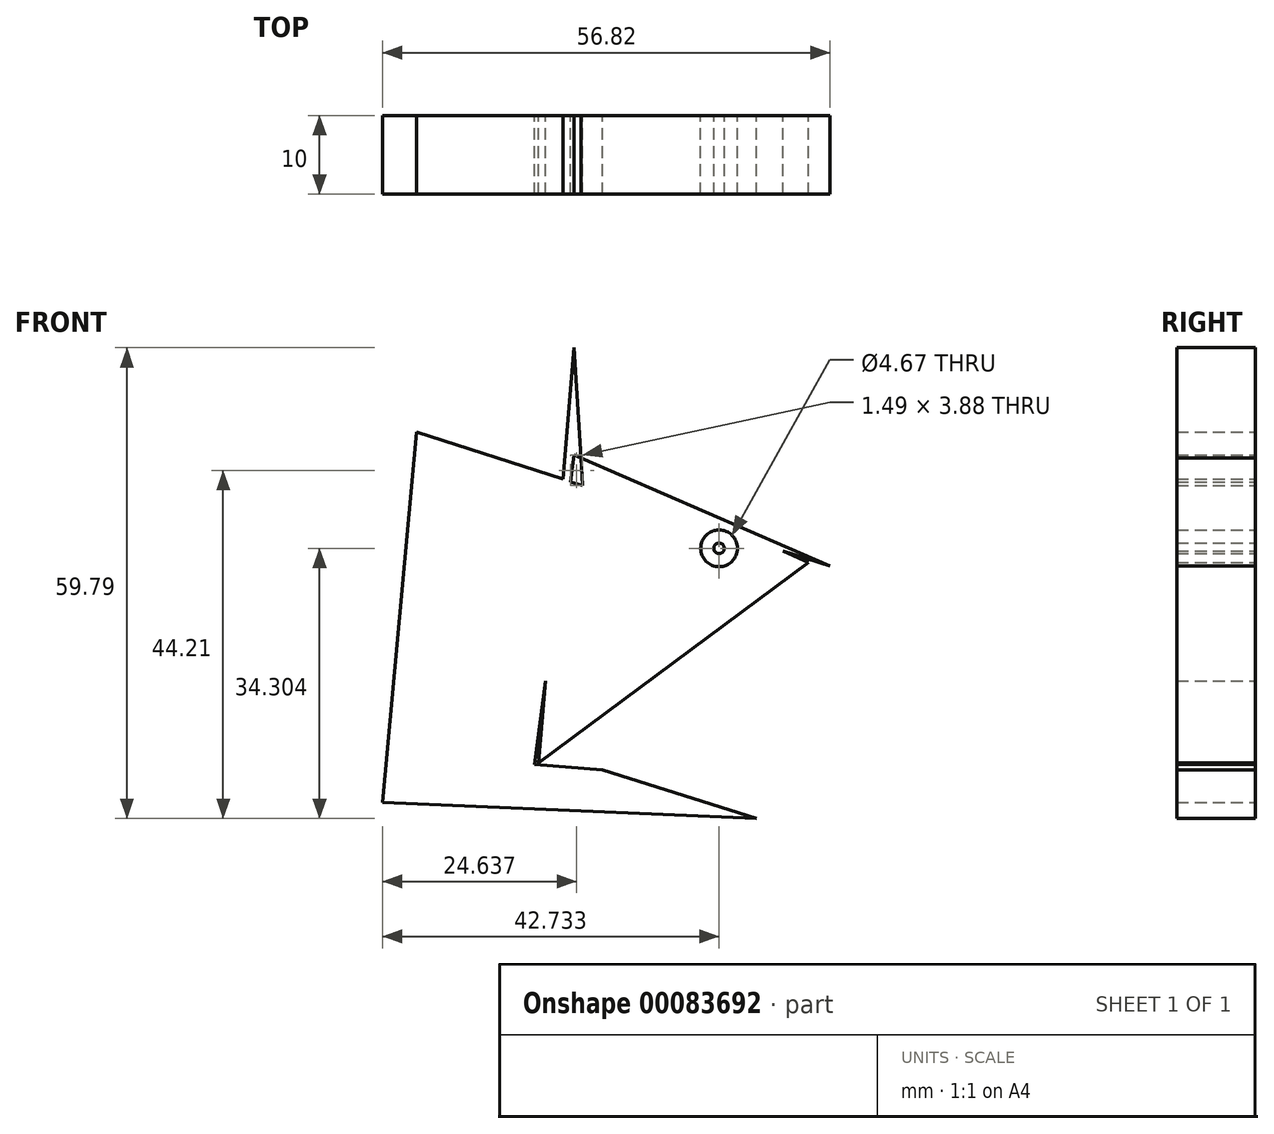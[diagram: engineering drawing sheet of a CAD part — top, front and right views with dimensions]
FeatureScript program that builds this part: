
annotation { "Feature Type Name" : "Feature", "Feature Type Description" : "" }
export const myFeature = defineFeature(function(context is Context, id is Id, definition is map)
    precondition{}
    {
        {
            var Q0;
            Q0=qCreatedBy(makeId("Front.planeOp"),FACE);
            var sketch = newSketch(context, id + "F0", { "sketchPlane" : qUnion([Q0])});
            skLineSegment(sketch, "E0", {"start": v(-28.64, 2.16) * mm, "end": v(-31.82, 54.67) * mm});
            skLineSegment(sketch, "E1", {"start": v(-31.82, 54.67) * mm, "end": v(-36.36, 1.93) * mm});
            skLineSegment(sketch, "E2", {"start": v(-36.36, 1.93) * mm, "end": v(-2.05, 27.4) * mm});
            skLineSegment(sketch, "E3", {"start": v(-2.05, 27.4) * mm, "end": v(-31.82, 41.03) * mm});
            skLineSegment(sketch, "E4", {"start": v(-31.82, 41.03) * mm, "end": v(0.68, 26.94) * mm});
            skLineSegment(sketch, "E5", {"start": v(0.68, 26.94) * mm, "end": v(-51.82, 43.99) * mm});
            skLineSegment(sketch, "E6", {"start": v(-51.82, 43.99) * mm, "end": v(-56.14, -3.07) * mm});
            skLineSegment(sketch, "E7", {"start": v(-56.14, -3.07) * mm, "end": v(-8.64, -5.12) * mm});
            skLineSegment(sketch, "E8", {"start": v(-8.64, -5.12) * mm, "end": v(-28.18, 1.02) * mm});
            skLineSegment(sketch, "E9", {"start": v(-28.18, 1.02) * mm, "end": v(-36.82, 1.7) * mm});
            skLineSegment(sketch, "E10", {"start": v(-36.82, 1.7) * mm, "end": v(-31.82, 41.03) * mm});
            skSolve(sketch);
        }
        {
            var Q0;
            Q0 = qSketchRegion(id + "F0", true);
            var Q1;
            Q1=sQuery(id+"F0.wireOp",EDGE,"E3");
            var Q2;
            Q2=sQuery(id+"F0.wireOp",EDGE,"E10");
            var Q3;
            Q3=sQuery(id+"F0.wireOp",EDGE,"E4");
            var Q4;
            Q4=sQuery(id+"F0.wireOp",EDGE,"E5");
            var Q5;
            Q5=sQuery(id+"F0.wireOp",EDGE,"E2");
            var Q6;
            Q6=sQuery(id+"F0.wireOp",EDGE,"E1");
            var Q7;
            Q7=sQuery(id+"F0.wireOp",EDGE,"E6");
            var Q8;
            Q8=sQuery(id+"F0.wireOp",EDGE,"E0");
            var Q9;
            Q9=sQuery(id+"F0.wireOp",EDGE,"E7");
            var Q10;
            Q10=sQuery(id+"F0.wireOp",EDGE,"E8");
            var Q11;
            Q11=sQuery(id+"F0.wireOp",EDGE,"E9");
            extrude(context, id + "F1", {"entities" : qUnion([Q0]), "surfaceEntities" : qUnion([Q1, Q2, Q3, Q4, Q5, Q6, Q7, Q8, Q9, Q10, Q11]), "depth" : 10 * mm});
        }
        {
            var Q0;
            Q0=qCreatedBy(makeId("Front.planeOp"),FACE);
            var sketch = newSketch(context, id + "F2", { "sketchPlane" : qUnion([Q0])});
            skCircle(sketch, "E11", {"center": v(-13.4, 29.18) * mm, "radius": 2.34 * mm});
            skCircle(sketch, "E12", {"center": v(-13.4, 29.18) * mm, "radius": 0.67 * mm});
            skSolve(sketch);
        }
        {
            var Q0;
            Q0 = qSketchRegion(id + "F2", true);
            var Q1;
            Q1=sQuery(id+"F2.wireOp",EDGE,"E12");
            var Q2;
            Q2=sQuery(id+"F2.wireOp",EDGE,"E11");
            extrude(context, id + "F3", {"entities" : qUnion([Q0]), "operationType" : NewBodyOperationType.REMOVE, "surfaceEntities" : qUnion([Q1, Q2]), "endBound" : BoundingType.THROUGH_ALL, "depth" : 25 * mm});
        }
    });
